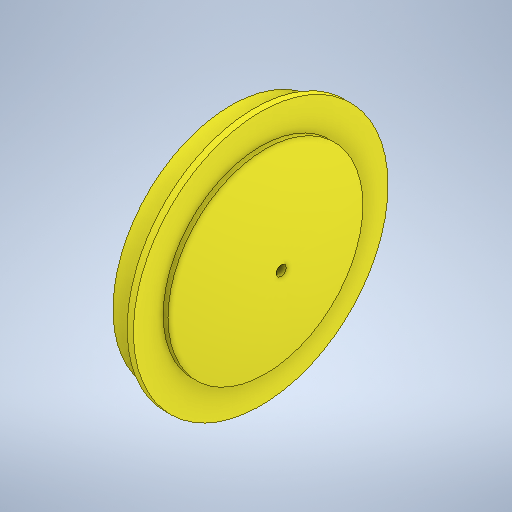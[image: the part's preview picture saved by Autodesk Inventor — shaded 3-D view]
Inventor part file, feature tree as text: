
AUTODESK INVENTOR PART (.ipt)
format: ipt  version: 2025.1 (Build 291241000, 241)  size: 293,888 bytes
history: native  units: mm
features: sketch x3, hole x2, revolve x1
ambient origin geometry x8: Origin, YZ Plane, XZ Plane, XY Plane, X Axis, Y Axis, Z Axis, Center Point
bodies: Solid1 (feature_tree)
feature tree (6):
  revolve  "Revolution1"  [1 undecoded]
  hole  "Hole1"  [1 undecoded]
  hole  "Hole2"  [1 undecoded]
  sketch  "Sketch1"  dims[d1=2.0mm d2=7.5mm]
  sketch  "Sketch2"  dims[d4=75.0mm d5=81.0mm]
  sketch  "Sketch3"  dims[d6=1.5mm d7=92.0mm d8=68.0mm d9=16.0mm d10=62.0mm d11=90.0deg d12=68.0mm d13=6.0mm d14=4.0mm d15=2.0mm d16=90.0deg d17=5.5mm d18=0.0mm d19=3.242mm d20=8.0mm d21=4.0mm d22=2.0mm d23=90.0deg d24=2.5mm d25=0.0mm]
note: 3 required parameter values undecoded (feature->parameter linkage not recoverable at this tier; creation-order binding heuristic only, values carry confidence <= 0.55)